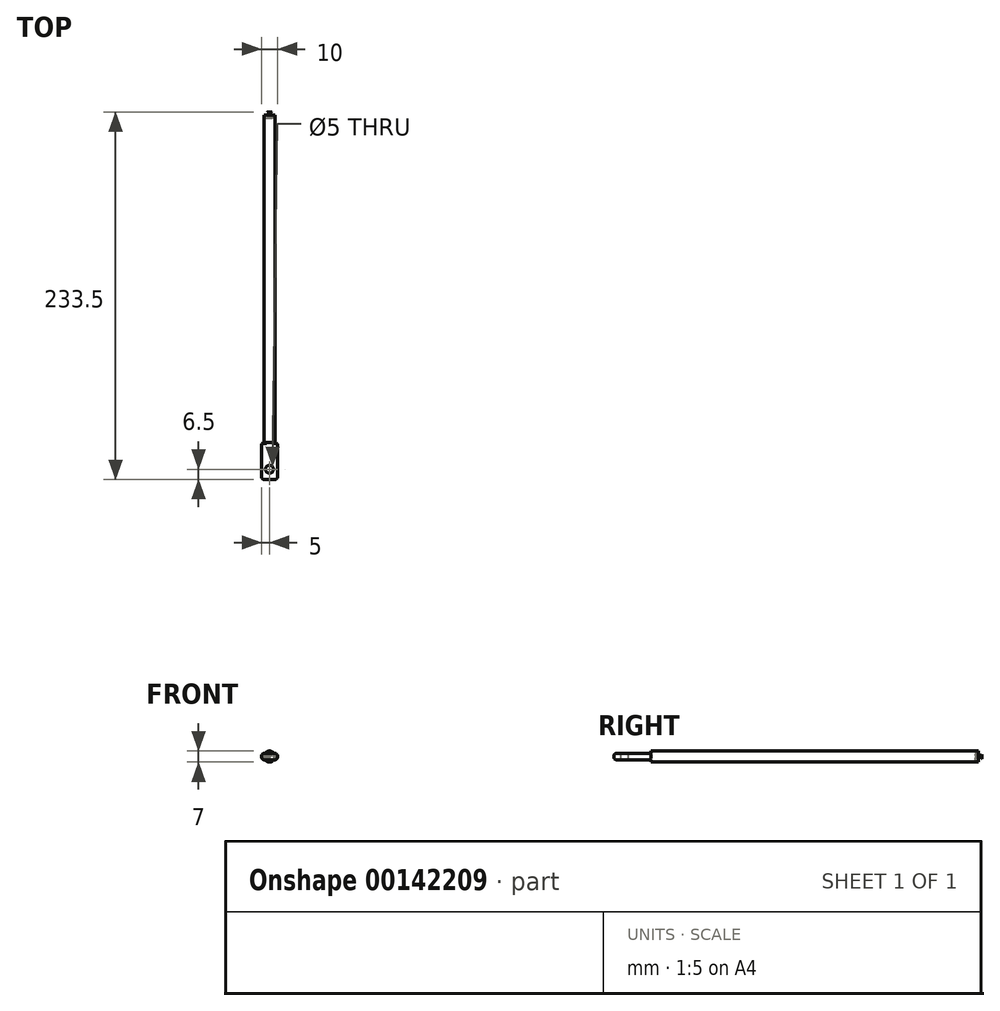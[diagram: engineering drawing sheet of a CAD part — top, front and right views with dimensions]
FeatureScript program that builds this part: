
annotation { "Feature Type Name" : "Feature", "Feature Type Description" : "" }
export const myFeature = defineFeature(function(context is Context, id is Id, definition is map)
    precondition{}
    {
        {
            var Q0;
            Q0=qCreatedBy(makeId("Top.planeOp"),FACE);
            var sketch = newSketch(context, id + "F0", { "sketchPlane" : qUnion([Q0])});
            skCircle(sketch, "E0", {"center": v(0, 0) * mm, "radius": 2.5 * mm});
            skLineSegment(sketch, "E1", {"start": v(0, 0) * mm, "end": v(0, -6.5) * mm, "construction": true});
            skLineSegment(sketch, "E2", {"start": v(-5, -6.5) * mm, "end": v(5, -6.5) * mm});
            skLineSegment(sketch, "E3", {"start": v(0, 0) * mm, "end": v(0, 17) * mm, "construction": true});
            skLineSegment(sketch, "E4", {"start": v(-3.5, 17) * mm, "end": v(3.5, 17) * mm});
            skPoint(sketch, "E5", {"position": v(0, 5.25) * mm});
            skLineSegment(sketch, "E6", {"start": v(5, -6.5) * mm, "end": v(5, 8.5) * mm});
            skPoint(sketch, "E7.visualSharp", {"position": v(5, 17) * mm});
            skLineSegment(sketch, "E8", {"start": v(5, 8.5) * mm, "end": v(5, 15.5) * mm});
            skArc(sketch, "E9", {"start": v(5, 15.5) * mm, "mid": v(4.56, 16.56) * mm, "end": v(3.5, 17) * mm});
            skLineSegment(sketch, "E10", {"start": v(-5, -6.5) * mm, "end": v(-5, 15.5) * mm});
            skArc(sketch, "E11", {"start": v(-3.5, 17) * mm, "mid": v(-4.56, 16.56) * mm, "end": v(-5, 15.5) * mm});
            skSolve(sketch);
        }
        {
            var Q0;
            Q0=qCreatedBy(makeId("Front.planeOp"),FACE);
            cPlane(context, id + "F1", {"entities" : qUnion([Q0]), "cplaneType" : CPlaneType.OFFSET, "offset" : 17 * mm, "oppositeDirection" : true, "width" : 150 * mm, "height" : 150 * mm});
        }
        {
            var Q0;
            Q0=qCreatedBy(id+"F1.planeOp",FACE);
            var sketch = newSketch(context, id + "F2", { "sketchPlane" : qUnion([Q0])});
            skPoint(sketch, "E12.0", {"position": v(0, 0) * mm});
            skCircle(sketch, "E13", {"center": v(0, 0) * mm, "radius": 3.5 * mm});
            skSolve(sketch);
        }
        {
            var Q0;
            Q0=qSketchRegion(id+"F2",true);
            extrude(context, id + "F3", {"entities" : qUnion([Q0]), "oppositeDirection" : true, "depth" : 210 * mm});
        }
        {
            var Q0;
            Q0=qSketchRegion(id+"F0",true);
            extrude(context, id + "F4", {"entities" : qUnion([Q0]), "operationType" : NewBodyOperationType.ADD, "depth" : 4 * mm, "symmetric" : true});
        }
        {
            var Q0;
            Q0=makeQuery(id+"F4.opExtrude","SWEPT_EDGE",EDGE,{"disambiguationData":[OSD([sQuery(id+"F0.wireOp",EDGE,"E2"),sQuery(id+"F0.wireOp",EDGE,"E6")])]});
            fillet(context, id + "F5", {"entities" : qUnion([Q0]), "radius" : 1.5 * mm, "tangentPropagation" : true, "allowEdgeOverflow" : false});
        }
        {
            var Q0;
            Q0=makeQuery(id+"F4.opExtrude","SWEPT_EDGE",EDGE,{"disambiguationData":[OSD([sQuery(id+"F0.wireOp",EDGE,"E2"),sQuery(id+"F0.wireOp",EDGE,"E10")])]});
            fillet(context, id + "F6", {"entities" : qUnion([Q0]), "radius" : 1.5 * mm, "tangentPropagation" : true, "allowEdgeOverflow" : false});
        }
        {
            var Q0;
            {var subQ0=sQuery(id+"F2.wireOp",EDGE,"E13");var subQ1=sQuery(id+"F0.wireOp",EDGE,"E4");Q0=makeQuery(id+"F4.boolean.opBoolean","SPLIT",EDGE,{"disambiguationData":[TD([makeQuery(id+"F3.opExtrude","SWEPT_FACE",FACE,{"disambiguationData":[OSD([subQ0])]}),makeQuery(id+"F3.opExtrude","CAP_FACE",FACE,{"disambiguationData":[OSD([subQ0])],"isStart":true}),makeQuery(id+"F4.opExtrude","CAP_FACE",FACE,{"disambiguationData":[OSD([sQuery(id+"F0.wireOp",EDGE,"E0"),sQuery(id+"F0.wireOp",EDGE,"E2"),subQ1,sQuery(id+"F0.wireOp",EDGE,"E6"),sQuery(id+"F0.wireOp",EDGE,"E8"),sQuery(id+"F0.wireOp",EDGE,"E9"),sQuery(id+"F0.wireOp",EDGE,"E10"),sQuery(id+"F0.wireOp",EDGE,"E11")])],"isStart":false}),makeQuery(id+"F4.opExtrude","SWEPT_FACE",FACE,{"disambiguationData":[OSD([subQ1])]})])],"derivedFrom":makeQuery(id+"F4.opExtrude","CAP_EDGE",EDGE,{"disambiguationData":[OSD([subQ1])],"isStart":false})});}
            fillet(context, id + "F7", {"entities" : qUnion([Q0]), "radius" : 1.5 * mm, "tangentPropagation" : true, "allowEdgeOverflow" : false});
        }
        {
            var Q0;
            {var subQ0=sQuery(id+"F2.wireOp",EDGE,"E13");var subQ1=sQuery(id+"F0.wireOp",EDGE,"E4");Q0=makeQuery(id+"F4.boolean.opBoolean","SPLIT",EDGE,{"disambiguationData":[TD([makeQuery(id+"F3.opExtrude","SWEPT_FACE",FACE,{"disambiguationData":[OSD([subQ0])]}),makeQuery(id+"F3.opExtrude","CAP_FACE",FACE,{"disambiguationData":[OSD([subQ0])],"isStart":true}),makeQuery(id+"F4.opExtrude","CAP_FACE",FACE,{"disambiguationData":[OSD([sQuery(id+"F0.wireOp",EDGE,"E0"),sQuery(id+"F0.wireOp",EDGE,"E2"),subQ1,sQuery(id+"F0.wireOp",EDGE,"E6"),sQuery(id+"F0.wireOp",EDGE,"E8"),sQuery(id+"F0.wireOp",EDGE,"E9"),sQuery(id+"F0.wireOp",EDGE,"E10"),sQuery(id+"F0.wireOp",EDGE,"E11")])],"isStart":true}),makeQuery(id+"F4.opExtrude","SWEPT_FACE",FACE,{"disambiguationData":[OSD([subQ1])]})])],"derivedFrom":makeQuery(id+"F4.opExtrude","CAP_EDGE",EDGE,{"disambiguationData":[OSD([subQ1])],"isStart":true})});}
            fillet(context, id + "F8", {"entities" : qUnion([Q0]), "radius" : 1.5 * mm, "tangentPropagation" : true, "allowEdgeOverflow" : false});
        }
        {
            var Q0;
            Q0=makeQuery(id+"F3.opExtrude","CAP_EDGE",EDGE,{"disambiguationData":[OSD([sQuery(id+"F2.wireOp",EDGE,"E13")])],"isStart":false});
            fillet(context, id + "F9", {"entities" : qUnion([Q0]), "radius" : 2 * mm, "tangentPropagation" : true, "allowEdgeOverflow" : false});
        }
    });
